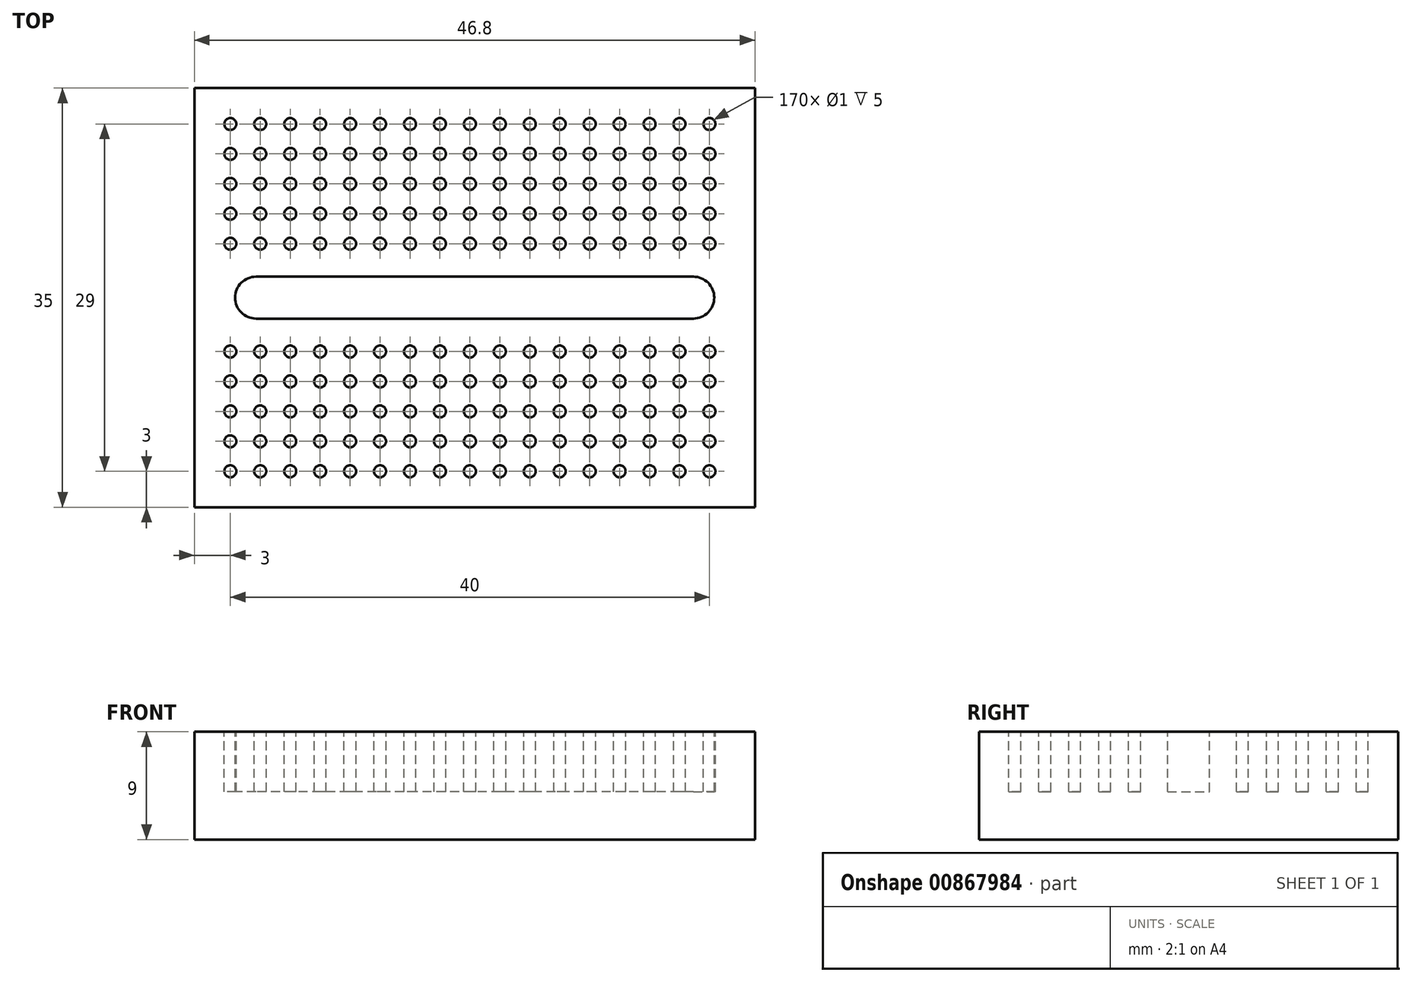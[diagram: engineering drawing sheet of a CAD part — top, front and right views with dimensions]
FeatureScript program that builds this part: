
annotation { "Feature Type Name" : "Feature", "Feature Type Description" : "" }
export const myFeature = defineFeature(function(context is Context, id is Id, definition is map)
    precondition{}
    {
        {
            var Q0;
            Q0=qCreatedBy(makeId("Top.planeOp"),FACE);
            var sketch = newSketch(context, id + "F0", { "sketchPlane" : qUnion([Q0])});
            skLineSegment(sketch, "E0.bottom", {"start": v(23.4, 17.5) * mm, "end": v(-23.4, 17.5) * mm});
            skLineSegment(sketch, "E0.top", {"start": v(23.4, -17.5) * mm, "end": v(-23.4, -17.5) * mm});
            skLineSegment(sketch, "E0.left", {"start": v(23.4, 17.5) * mm, "end": v(23.4, -17.5) * mm});
            skLineSegment(sketch, "E0.right", {"start": v(-23.4, 17.5) * mm, "end": v(-23.4, -17.5) * mm});
            skPoint(sketch, "E0.middle", {"position": v(0, 0) * mm});
            skSolve(sketch);
        }
        {
            var Q0;
            Q0 = qSketchRegion(id + "F0", true);
            extrude(context, id + "F1", {"entities" : qUnion([Q0]), "depth" : 9 * mm, "offsetDistance" : 25 * mm});
        }
        {
            var Q0;
            Q0=makeQuery(id+"F1.opExtrude","CAP_FACE",FACE,{"disambiguationData":[OSD([sQuery(id+"F0.wireOp",EDGE,"E0.bottom"),sQuery(id+"F0.wireOp",EDGE,"E0.top"),sQuery(id+"F0.wireOp",EDGE,"E0.left"),sQuery(id+"F0.wireOp",EDGE,"E0.right")])],"isStart":false});
            var sketch = newSketch(context, id + "F2", { "sketchPlane" : qUnion([Q0])});
            skLineSegment(sketch, "E1.bottom", {"start": v(18.25, 1.75) * mm, "end": v(-18.25, 1.75) * mm});
            skLineSegment(sketch, "E1.top", {"start": v(18.25, -1.75) * mm, "end": v(-18.25, -1.75) * mm});
            skLineSegment(sketch, "E1.left", {"start": v(18.25, 1.75) * mm, "end": v(18.25, -1.75) * mm});
            skLineSegment(sketch, "E1.right", {"start": v(-18.25, 1.75) * mm, "end": v(-18.25, -1.75) * mm});
            skPoint(sketch, "E1.middle", {"position": v(0, 0) * mm});
            skCircle(sketch, "E2", {"center": v(-18.25, 0) * mm, "radius": 1.75 * mm});
            skCircle(sketch, "E3", {"center": v(18.25, 0) * mm, "radius": 1.75 * mm});
            skCircle(sketch, "E4", {"center": v(-20.4, 14.5) * mm, "radius": 0.5 * mm});
            skCircle(sketch, "E5", {"center": v(-20.4, -14.5) * mm, "radius": 0.5 * mm});
            skCircle(sketch, "E6.0.1.0", {"center": v(-20.4, -12) * mm, "radius": 0.5 * mm});
            skCircle(sketch, "E6.0.2.0", {"center": v(-20.4, -9.5) * mm, "radius": 0.5 * mm});
            skCircle(sketch, "E6.0.3.0", {"center": v(-20.4, -7) * mm, "radius": 0.5 * mm});
            skCircle(sketch, "E6.0.4.0", {"center": v(-20.4, -4.5) * mm, "radius": 0.5 * mm});
            skCircle(sketch, "E6.1.0.0", {"center": v(-17.9, -14.5) * mm, "radius": 0.5 * mm});
            skCircle(sketch, "E6.1.1.0", {"center": v(-17.9, -12) * mm, "radius": 0.5 * mm});
            skCircle(sketch, "E6.1.2.0", {"center": v(-17.9, -9.5) * mm, "radius": 0.5 * mm});
            skCircle(sketch, "E6.1.3.0", {"center": v(-17.9, -7) * mm, "radius": 0.5 * mm});
            skCircle(sketch, "E6.1.4.0", {"center": v(-17.9, -4.5) * mm, "radius": 0.5 * mm});
            skCircle(sketch, "E6.2.0.0", {"center": v(-15.4, -14.5) * mm, "radius": 0.5 * mm});
            skCircle(sketch, "E6.2.1.0", {"center": v(-15.4, -12) * mm, "radius": 0.5 * mm});
            skCircle(sketch, "E6.2.2.0", {"center": v(-15.4, -9.5) * mm, "radius": 0.5 * mm});
            skCircle(sketch, "E6.2.3.0", {"center": v(-15.4, -7) * mm, "radius": 0.5 * mm});
            skCircle(sketch, "E6.2.4.0", {"center": v(-15.4, -4.5) * mm, "radius": 0.5 * mm});
            skCircle(sketch, "E6.3.0.0", {"center": v(-12.9, -14.5) * mm, "radius": 0.5 * mm});
            skCircle(sketch, "E6.3.1.0", {"center": v(-12.9, -12) * mm, "radius": 0.5 * mm});
            skCircle(sketch, "E6.3.2.0", {"center": v(-12.9, -9.5) * mm, "radius": 0.5 * mm});
            skCircle(sketch, "E6.3.3.0", {"center": v(-12.9, -7) * mm, "radius": 0.5 * mm});
            skCircle(sketch, "E6.3.4.0", {"center": v(-12.9, -4.5) * mm, "radius": 0.5 * mm});
            skCircle(sketch, "E6.4.0.0", {"center": v(-10.4, -14.5) * mm, "radius": 0.5 * mm});
            skCircle(sketch, "E6.4.1.0", {"center": v(-10.4, -12) * mm, "radius": 0.5 * mm});
            skCircle(sketch, "E6.4.2.0", {"center": v(-10.4, -9.5) * mm, "radius": 0.5 * mm});
            skCircle(sketch, "E6.4.3.0", {"center": v(-10.4, -7) * mm, "radius": 0.5 * mm});
            skCircle(sketch, "E6.4.4.0", {"center": v(-10.4, -4.5) * mm, "radius": 0.5 * mm});
            skCircle(sketch, "E6.5.0.0", {"center": v(-7.9, -14.5) * mm, "radius": 0.5 * mm});
            skCircle(sketch, "E6.5.1.0", {"center": v(-7.9, -12) * mm, "radius": 0.5 * mm});
            skCircle(sketch, "E6.5.2.0", {"center": v(-7.9, -9.5) * mm, "radius": 0.5 * mm});
            skCircle(sketch, "E6.5.3.0", {"center": v(-7.9, -7) * mm, "radius": 0.5 * mm});
            skCircle(sketch, "E6.5.4.0", {"center": v(-7.9, -4.5) * mm, "radius": 0.5 * mm});
            skCircle(sketch, "E6.6.0.0", {"center": v(-5.4, -14.5) * mm, "radius": 0.5 * mm});
            skCircle(sketch, "E6.6.1.0", {"center": v(-5.4, -12) * mm, "radius": 0.5 * mm});
            skCircle(sketch, "E6.6.2.0", {"center": v(-5.4, -9.5) * mm, "radius": 0.5 * mm});
            skCircle(sketch, "E6.6.3.0", {"center": v(-5.4, -7) * mm, "radius": 0.5 * mm});
            skCircle(sketch, "E6.6.4.0", {"center": v(-5.4, -4.5) * mm, "radius": 0.5 * mm});
            skCircle(sketch, "E6.7.0.0", {"center": v(-2.9, -14.5) * mm, "radius": 0.5 * mm});
            skCircle(sketch, "E6.7.1.0", {"center": v(-2.9, -12) * mm, "radius": 0.5 * mm});
            skCircle(sketch, "E6.7.2.0", {"center": v(-2.9, -9.5) * mm, "radius": 0.5 * mm});
            skCircle(sketch, "E6.7.3.0", {"center": v(-2.9, -7) * mm, "radius": 0.5 * mm});
            skCircle(sketch, "E6.7.4.0", {"center": v(-2.9, -4.5) * mm, "radius": 0.5 * mm});
            skCircle(sketch, "E6.8.0.0", {"center": v(-0.4, -14.5) * mm, "radius": 0.5 * mm});
            skCircle(sketch, "E6.8.1.0", {"center": v(-0.4, -12) * mm, "radius": 0.5 * mm});
            skCircle(sketch, "E6.8.2.0", {"center": v(-0.4, -9.5) * mm, "radius": 0.5 * mm});
            skCircle(sketch, "E6.8.3.0", {"center": v(-0.4, -7) * mm, "radius": 0.5 * mm});
            skCircle(sketch, "E6.8.4.0", {"center": v(-0.4, -4.5) * mm, "radius": 0.5 * mm});
            skCircle(sketch, "E6.9.0.0", {"center": v(2.1, -14.5) * mm, "radius": 0.5 * mm});
            skCircle(sketch, "E6.9.1.0", {"center": v(2.1, -12) * mm, "radius": 0.5 * mm});
            skCircle(sketch, "E6.9.2.0", {"center": v(2.1, -9.5) * mm, "radius": 0.5 * mm});
            skCircle(sketch, "E6.9.3.0", {"center": v(2.1, -7) * mm, "radius": 0.5 * mm});
            skCircle(sketch, "E6.9.4.0", {"center": v(2.1, -4.5) * mm, "radius": 0.5 * mm});
            skCircle(sketch, "E6.10.0.0", {"center": v(4.6, -14.5) * mm, "radius": 0.5 * mm});
            skCircle(sketch, "E6.10.1.0", {"center": v(4.6, -12) * mm, "radius": 0.5 * mm});
            skCircle(sketch, "E6.10.2.0", {"center": v(4.6, -9.5) * mm, "radius": 0.5 * mm});
            skCircle(sketch, "E6.10.3.0", {"center": v(4.6, -7) * mm, "radius": 0.5 * mm});
            skCircle(sketch, "E6.10.4.0", {"center": v(4.6, -4.5) * mm, "radius": 0.5 * mm});
            skCircle(sketch, "E6.11.0.0", {"center": v(7.1, -14.5) * mm, "radius": 0.5 * mm});
            skCircle(sketch, "E6.11.1.0", {"center": v(7.1, -12) * mm, "radius": 0.5 * mm});
            skCircle(sketch, "E6.11.2.0", {"center": v(7.1, -9.5) * mm, "radius": 0.5 * mm});
            skCircle(sketch, "E6.11.3.0", {"center": v(7.1, -7) * mm, "radius": 0.5 * mm});
            skCircle(sketch, "E6.11.4.0", {"center": v(7.1, -4.5) * mm, "radius": 0.5 * mm});
            skCircle(sketch, "E6.12.0.0", {"center": v(9.6, -14.5) * mm, "radius": 0.5 * mm});
            skCircle(sketch, "E6.12.1.0", {"center": v(9.6, -12) * mm, "radius": 0.5 * mm});
            skCircle(sketch, "E6.12.2.0", {"center": v(9.6, -9.5) * mm, "radius": 0.5 * mm});
            skCircle(sketch, "E6.12.3.0", {"center": v(9.6, -7) * mm, "radius": 0.5 * mm});
            skCircle(sketch, "E6.12.4.0", {"center": v(9.6, -4.5) * mm, "radius": 0.5 * mm});
            skCircle(sketch, "E6.13.0.0", {"center": v(12.1, -14.5) * mm, "radius": 0.5 * mm});
            skCircle(sketch, "E6.13.1.0", {"center": v(12.1, -12) * mm, "radius": 0.5 * mm});
            skCircle(sketch, "E6.13.2.0", {"center": v(12.1, -9.5) * mm, "radius": 0.5 * mm});
            skCircle(sketch, "E6.13.3.0", {"center": v(12.1, -7) * mm, "radius": 0.5 * mm});
            skCircle(sketch, "E6.13.4.0", {"center": v(12.1, -4.5) * mm, "radius": 0.5 * mm});
            skCircle(sketch, "E6.14.0.0", {"center": v(14.6, -14.5) * mm, "radius": 0.5 * mm});
            skCircle(sketch, "E6.14.1.0", {"center": v(14.6, -12) * mm, "radius": 0.5 * mm});
            skCircle(sketch, "E6.14.2.0", {"center": v(14.6, -9.5) * mm, "radius": 0.5 * mm});
            skCircle(sketch, "E6.14.3.0", {"center": v(14.6, -7) * mm, "radius": 0.5 * mm});
            skCircle(sketch, "E6.14.4.0", {"center": v(14.6, -4.5) * mm, "radius": 0.5 * mm});
            skCircle(sketch, "E6.15.0.0", {"center": v(17.1, -14.5) * mm, "radius": 0.5 * mm});
            skCircle(sketch, "E6.15.1.0", {"center": v(17.1, -12) * mm, "radius": 0.5 * mm});
            skCircle(sketch, "E6.15.2.0", {"center": v(17.1, -9.5) * mm, "radius": 0.5 * mm});
            skCircle(sketch, "E6.15.3.0", {"center": v(17.1, -7) * mm, "radius": 0.5 * mm});
            skCircle(sketch, "E6.15.4.0", {"center": v(17.1, -4.5) * mm, "radius": 0.5 * mm});
            skCircle(sketch, "E6.16.0.0", {"center": v(19.6, -14.5) * mm, "radius": 0.5 * mm});
            skCircle(sketch, "E6.16.1.0", {"center": v(19.6, -12) * mm, "radius": 0.5 * mm});
            skCircle(sketch, "E6.16.2.0", {"center": v(19.6, -9.5) * mm, "radius": 0.5 * mm});
            skCircle(sketch, "E6.16.3.0", {"center": v(19.6, -7) * mm, "radius": 0.5 * mm});
            skCircle(sketch, "E6.16.4.0", {"center": v(19.6, -4.5) * mm, "radius": 0.5 * mm});
            skLineSegment(sketch, "E6.direction1", {"start": v(-20.4, -14.5) * mm, "end": v(-17.9, -14.5) * mm, "construction": true});
            skLineSegment(sketch, "E6.direction2", {"start": v(-20.4, -14.5) * mm, "end": v(-20.4, -12) * mm, "construction": true});
            skCircle(sketch, "E7.0.1.0", {"center": v(-20.4, 12) * mm, "radius": 0.5 * mm});
            skCircle(sketch, "E7.0.2.0", {"center": v(-20.4, 9.5) * mm, "radius": 0.5 * mm});
            skCircle(sketch, "E7.0.3.0", {"center": v(-20.4, 7) * mm, "radius": 0.5 * mm});
            skCircle(sketch, "E7.0.4.0", {"center": v(-20.4, 4.5) * mm, "radius": 0.5 * mm});
            skCircle(sketch, "E7.1.0.0", {"center": v(-17.9, 14.5) * mm, "radius": 0.5 * mm});
            skCircle(sketch, "E7.1.1.0", {"center": v(-17.9, 12) * mm, "radius": 0.5 * mm});
            skCircle(sketch, "E7.1.2.0", {"center": v(-17.9, 9.5) * mm, "radius": 0.5 * mm});
            skCircle(sketch, "E7.1.3.0", {"center": v(-17.9, 7) * mm, "radius": 0.5 * mm});
            skCircle(sketch, "E7.1.4.0", {"center": v(-17.9, 4.5) * mm, "radius": 0.5 * mm});
            skCircle(sketch, "E7.2.0.0", {"center": v(-15.4, 14.5) * mm, "radius": 0.5 * mm});
            skCircle(sketch, "E7.2.1.0", {"center": v(-15.4, 12) * mm, "radius": 0.5 * mm});
            skCircle(sketch, "E7.2.2.0", {"center": v(-15.4, 9.5) * mm, "radius": 0.5 * mm});
            skCircle(sketch, "E7.2.3.0", {"center": v(-15.4, 7) * mm, "radius": 0.5 * mm});
            skCircle(sketch, "E7.2.4.0", {"center": v(-15.4, 4.5) * mm, "radius": 0.5 * mm});
            skCircle(sketch, "E7.3.0.0", {"center": v(-12.9, 14.5) * mm, "radius": 0.5 * mm});
            skCircle(sketch, "E7.3.1.0", {"center": v(-12.9, 12) * mm, "radius": 0.5 * mm});
            skCircle(sketch, "E7.3.2.0", {"center": v(-12.9, 9.5) * mm, "radius": 0.5 * mm});
            skCircle(sketch, "E7.3.3.0", {"center": v(-12.9, 7) * mm, "radius": 0.5 * mm});
            skCircle(sketch, "E7.3.4.0", {"center": v(-12.9, 4.5) * mm, "radius": 0.5 * mm});
            skCircle(sketch, "E7.4.0.0", {"center": v(-10.4, 14.5) * mm, "radius": 0.5 * mm});
            skCircle(sketch, "E7.4.1.0", {"center": v(-10.4, 12) * mm, "radius": 0.5 * mm});
            skCircle(sketch, "E7.4.2.0", {"center": v(-10.4, 9.5) * mm, "radius": 0.5 * mm});
            skCircle(sketch, "E7.4.3.0", {"center": v(-10.4, 7) * mm, "radius": 0.5 * mm});
            skCircle(sketch, "E7.4.4.0", {"center": v(-10.4, 4.5) * mm, "radius": 0.5 * mm});
            skCircle(sketch, "E7.5.0.0", {"center": v(-7.9, 14.5) * mm, "radius": 0.5 * mm});
            skCircle(sketch, "E7.5.1.0", {"center": v(-7.9, 12) * mm, "radius": 0.5 * mm});
            skCircle(sketch, "E7.5.2.0", {"center": v(-7.9, 9.5) * mm, "radius": 0.5 * mm});
            skCircle(sketch, "E7.5.3.0", {"center": v(-7.9, 7) * mm, "radius": 0.5 * mm});
            skCircle(sketch, "E7.5.4.0", {"center": v(-7.9, 4.5) * mm, "radius": 0.5 * mm});
            skCircle(sketch, "E7.6.0.0", {"center": v(-5.4, 14.5) * mm, "radius": 0.5 * mm});
            skCircle(sketch, "E7.6.1.0", {"center": v(-5.4, 12) * mm, "radius": 0.5 * mm});
            skCircle(sketch, "E7.6.2.0", {"center": v(-5.4, 9.5) * mm, "radius": 0.5 * mm});
            skCircle(sketch, "E7.6.3.0", {"center": v(-5.4, 7) * mm, "radius": 0.5 * mm});
            skCircle(sketch, "E7.6.4.0", {"center": v(-5.4, 4.5) * mm, "radius": 0.5 * mm});
            skCircle(sketch, "E7.7.0.0", {"center": v(-2.9, 14.5) * mm, "radius": 0.5 * mm});
            skCircle(sketch, "E7.7.1.0", {"center": v(-2.9, 12) * mm, "radius": 0.5 * mm});
            skCircle(sketch, "E7.7.2.0", {"center": v(-2.9, 9.5) * mm, "radius": 0.5 * mm});
            skCircle(sketch, "E7.7.3.0", {"center": v(-2.9, 7) * mm, "radius": 0.5 * mm});
            skCircle(sketch, "E7.7.4.0", {"center": v(-2.9, 4.5) * mm, "radius": 0.5 * mm});
            skCircle(sketch, "E7.8.0.0", {"center": v(-0.4, 14.5) * mm, "radius": 0.5 * mm});
            skCircle(sketch, "E7.8.1.0", {"center": v(-0.4, 12) * mm, "radius": 0.5 * mm});
            skCircle(sketch, "E7.8.2.0", {"center": v(-0.4, 9.5) * mm, "radius": 0.5 * mm});
            skCircle(sketch, "E7.8.3.0", {"center": v(-0.4, 7) * mm, "radius": 0.5 * mm});
            skCircle(sketch, "E7.8.4.0", {"center": v(-0.4, 4.5) * mm, "radius": 0.5 * mm});
            skCircle(sketch, "E7.9.0.0", {"center": v(2.1, 14.5) * mm, "radius": 0.5 * mm});
            skCircle(sketch, "E7.9.1.0", {"center": v(2.1, 12) * mm, "radius": 0.5 * mm});
            skCircle(sketch, "E7.9.2.0", {"center": v(2.1, 9.5) * mm, "radius": 0.5 * mm});
            skCircle(sketch, "E7.9.3.0", {"center": v(2.1, 7) * mm, "radius": 0.5 * mm});
            skCircle(sketch, "E7.9.4.0", {"center": v(2.1, 4.5) * mm, "radius": 0.5 * mm});
            skCircle(sketch, "E7.10.0.0", {"center": v(4.6, 14.5) * mm, "radius": 0.5 * mm});
            skCircle(sketch, "E7.10.1.0", {"center": v(4.6, 12) * mm, "radius": 0.5 * mm});
            skCircle(sketch, "E7.10.2.0", {"center": v(4.6, 9.5) * mm, "radius": 0.5 * mm});
            skCircle(sketch, "E7.10.3.0", {"center": v(4.6, 7) * mm, "radius": 0.5 * mm});
            skCircle(sketch, "E7.10.4.0", {"center": v(4.6, 4.5) * mm, "radius": 0.5 * mm});
            skCircle(sketch, "E7.11.0.0", {"center": v(7.1, 14.5) * mm, "radius": 0.5 * mm});
            skCircle(sketch, "E7.11.1.0", {"center": v(7.1, 12) * mm, "radius": 0.5 * mm});
            skCircle(sketch, "E7.11.2.0", {"center": v(7.1, 9.5) * mm, "radius": 0.5 * mm});
            skCircle(sketch, "E7.11.3.0", {"center": v(7.1, 7) * mm, "radius": 0.5 * mm});
            skCircle(sketch, "E7.11.4.0", {"center": v(7.1, 4.5) * mm, "radius": 0.5 * mm});
            skCircle(sketch, "E7.12.0.0", {"center": v(9.6, 14.5) * mm, "radius": 0.5 * mm});
            skCircle(sketch, "E7.12.1.0", {"center": v(9.6, 12) * mm, "radius": 0.5 * mm});
            skCircle(sketch, "E7.12.2.0", {"center": v(9.6, 9.5) * mm, "radius": 0.5 * mm});
            skCircle(sketch, "E7.12.3.0", {"center": v(9.6, 7) * mm, "radius": 0.5 * mm});
            skCircle(sketch, "E7.12.4.0", {"center": v(9.6, 4.5) * mm, "radius": 0.5 * mm});
            skCircle(sketch, "E7.13.0.0", {"center": v(12.1, 14.5) * mm, "radius": 0.5 * mm});
            skCircle(sketch, "E7.13.1.0", {"center": v(12.1, 12) * mm, "radius": 0.5 * mm});
            skCircle(sketch, "E7.13.2.0", {"center": v(12.1, 9.5) * mm, "radius": 0.5 * mm});
            skCircle(sketch, "E7.13.3.0", {"center": v(12.1, 7) * mm, "radius": 0.5 * mm});
            skCircle(sketch, "E7.13.4.0", {"center": v(12.1, 4.5) * mm, "radius": 0.5 * mm});
            skCircle(sketch, "E7.14.0.0", {"center": v(14.6, 14.5) * mm, "radius": 0.5 * mm});
            skCircle(sketch, "E7.14.1.0", {"center": v(14.6, 12) * mm, "radius": 0.5 * mm});
            skCircle(sketch, "E7.14.2.0", {"center": v(14.6, 9.5) * mm, "radius": 0.5 * mm});
            skCircle(sketch, "E7.14.3.0", {"center": v(14.6, 7) * mm, "radius": 0.5 * mm});
            skCircle(sketch, "E7.14.4.0", {"center": v(14.6, 4.5) * mm, "radius": 0.5 * mm});
            skCircle(sketch, "E7.15.0.0", {"center": v(17.1, 14.5) * mm, "radius": 0.5 * mm});
            skCircle(sketch, "E7.15.1.0", {"center": v(17.1, 12) * mm, "radius": 0.5 * mm});
            skCircle(sketch, "E7.15.2.0", {"center": v(17.1, 9.5) * mm, "radius": 0.5 * mm});
            skCircle(sketch, "E7.15.3.0", {"center": v(17.1, 7) * mm, "radius": 0.5 * mm});
            skCircle(sketch, "E7.15.4.0", {"center": v(17.1, 4.5) * mm, "radius": 0.5 * mm});
            skCircle(sketch, "E7.16.0.0", {"center": v(19.6, 14.5) * mm, "radius": 0.5 * mm});
            skCircle(sketch, "E7.16.1.0", {"center": v(19.6, 12) * mm, "radius": 0.5 * mm});
            skCircle(sketch, "E7.16.2.0", {"center": v(19.6, 9.5) * mm, "radius": 0.5 * mm});
            skCircle(sketch, "E7.16.3.0", {"center": v(19.6, 7) * mm, "radius": 0.5 * mm});
            skCircle(sketch, "E7.16.4.0", {"center": v(19.6, 4.5) * mm, "radius": 0.5 * mm});
            skLineSegment(sketch, "E7.direction1", {"start": v(-20.4, 14.5) * mm, "end": v(-17.9, 14.5) * mm, "construction": true});
            skLineSegment(sketch, "E7.direction2", {"start": v(-20.4, 14.5) * mm, "end": v(-20.4, 12) * mm, "construction": true});
            skSolve(sketch);
        }
        {
            var Q0;
            Q0 = qSketchRegion(id + "F2", true);
            extrude(context, id + "F3", {"entities" : qUnion([Q0]), "operationType" : NewBodyOperationType.REMOVE, "oppositeDirection" : true, "depth" : 5 * mm, "offsetDistance" : 25 * mm});
        }
    });
